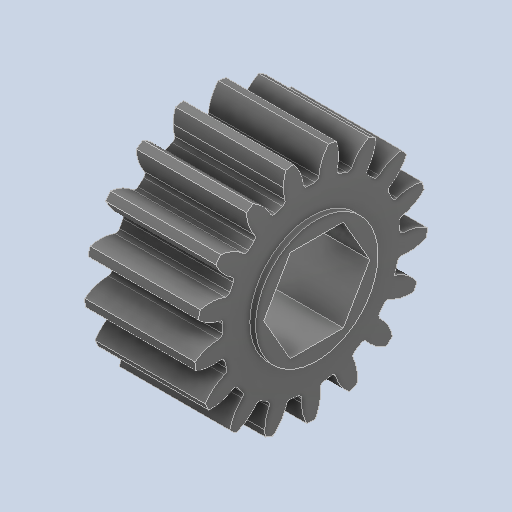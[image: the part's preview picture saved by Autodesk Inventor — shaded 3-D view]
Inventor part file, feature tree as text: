
AUTODESK INVENTOR PART (.ipt)
format: ipt  version: 2024.2 (Build 282272000, 272)  size: 289,792 bytes
history: native  units: in
note: dims shown in document units (in); Inventor stores cm internally (conversion verified against a paired STEP export)
features: fillet x1
ambient origin geometry x8: Origin, YZ Plane, XZ Plane, XY Plane, X Axis, Y Axis, Z Axis, Center Point
bodies: Solid1 (feature_tree)
feature tree (1):
  fillet  "Fillet1"  [1 undecoded]
note: 1 required parameter value undecoded (feature->parameter linkage not recoverable at this tier; creation-order binding heuristic only, values carry confidence <= 0.55)
